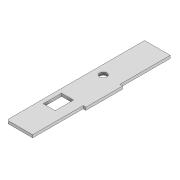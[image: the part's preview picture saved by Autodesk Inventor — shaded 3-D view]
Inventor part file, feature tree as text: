
AUTODESK INVENTOR PART (.ipt)
format: ipt  version: 2020 (Build 240168000, 168)  size: 113,152 bytes
history: native  units: mm
features: extrude x3, sketch x3, fillet x1
ambient origin geometry x8: Origin, YZ Plane, XZ Plane, XY Plane, X Axis, Y Axis, Z Axis, Center Point
bodies: Solid1 (feature_tree)
feature tree (7):
  extrude  "Extrusion1"  Depth=3.0mm
  extrude  "Extrusion3"  Depth=28.0mm
  extrude  "Extrusion4"  Depth=2.0mm
  fillet  "Fillet1"  Radius=18.0mm
  sketch  "Sketch1"  dims[d0=150.0mm d1=3.0mm]
  sketch  "Sketch3"  dims[d2=40.0mm d3=28.0mm]
  sketch  "Sketch4"  dims[d4=3.0mm d5=0.0mm d18=7.8mm d20=18.0mm d22=3.0mm d23=0.0mm d24=55.0mm d25=20.0mm d26=13.0mm d27=45.0mm d28=10.0mm d29=0.0mm d30=2.0mm]
